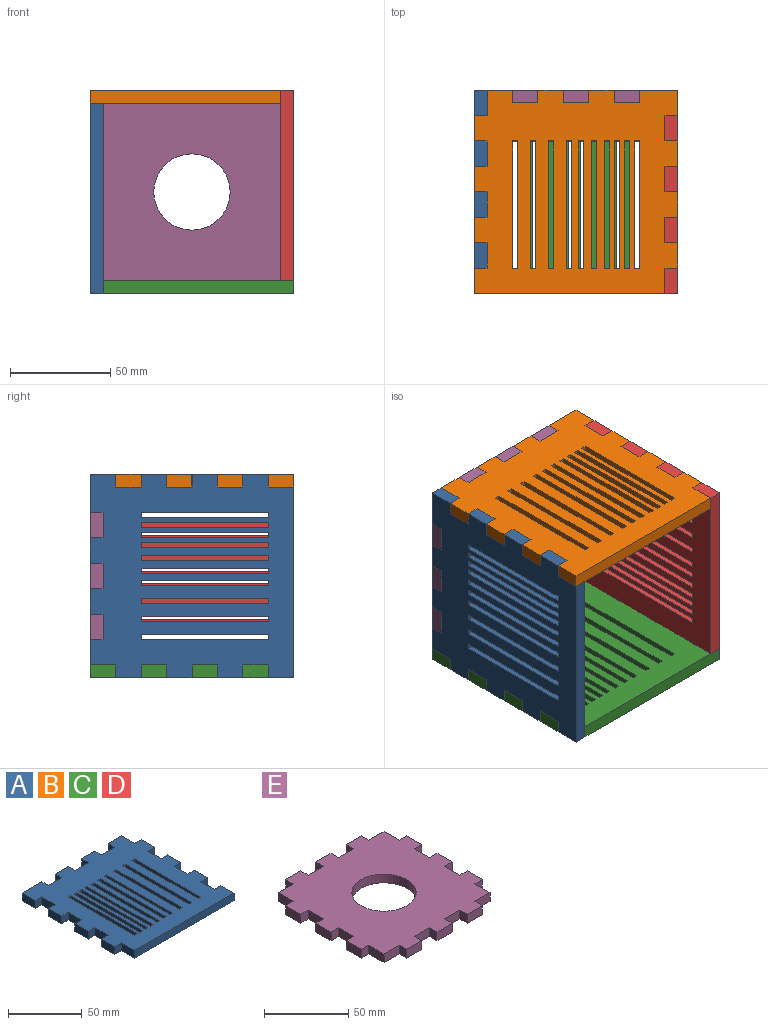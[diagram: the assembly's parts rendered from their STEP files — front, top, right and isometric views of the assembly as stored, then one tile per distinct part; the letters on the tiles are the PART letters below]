
ASSEMBLY  parts=5 mates=4
PART A: 86 faces, bbox 101.6x101.6x6.4 mm
  f0: plane 101.6x101.6mm, normal (0,0,1), area 7822.6mm2, adj f2,f3,f4,f5,f6,f7,f8,f9
  f1: plane 101.6x101.6mm, normal (0,0,-1), area 7822.6mm2, adj f2,f3,f4,f5,f6,f7,f8,f9
  f2: plane 6.35x6.35mm, normal (0,1,0), area 40.3mm2, adj f0,f1,f3,f45
  f3: plane 12.7x6.35mm, normal (1,0,0), area 80.6mm2, adj f0,f1,f2,f4
  f4: plane 6.35x6.35mm, normal (0,-1,0), area 40.3mm2, adj f0,f1,f3,f5
  f5: plane 12.7x6.35mm, normal (1,0,0), area 80.6mm2, adj f0,f1,f4,f6
  f6: plane 6.35x6.35mm, normal (0,1,0), area 40.3mm2, adj f0,f1,f5,f7
  f7: plane 12.7x6.35mm, normal (1,0,0), area 80.6mm2, adj f0,f1,f6,f8
  f8: plane 6.35x6.35mm, normal (0,-1,0), area 40.3mm2, adj f0,f1,f7,f9
  f9: plane 12.7x6.35mm, normal (1,0,0), area 80.6mm2, adj f0,f1,f8,f10
  f10: plane 6.35x6.35mm, normal (0,1,0), area 40.3mm2, adj f0,f1,f9,f11
  f11: plane 12.7x6.35mm, normal (1,0,0), area 80.6mm2, adj f0,f1,f10,f12
  f12: plane 6.35x6.35mm, normal (0,-1,0), area 40.3mm2, adj f0,f1,f11,f13
  f13: plane 12.7x6.35mm, normal (1,0,0), area 80.6mm2, adj f0,f1,f12,f14
  f14: plane 6.35x6.35mm, normal (0,1,0), area 40.3mm2, adj f0,f1,f13,f15
  f15: plane 12.7x6.35mm, normal (1,0,0), area 80.6mm2, adj f0,f1,f14,f16
  f16: plane 12.7x6.35mm, normal (0,1,0), area 80.6mm2, adj f0,f1,f15,f17
  f17: plane 6.35x6.35mm, normal (-1,0,0), area 40.3mm2, adj f0,f1,f16,f18
  f18: plane 12.7x6.35mm, normal (0,1,0), area 80.6mm2, adj f0,f1,f17,f19
  f19: plane 6.35x6.35mm, normal (1,0,0), area 40.3mm2, adj f0,f1,f18,f20
  f20: plane 12.7x6.35mm, normal (0,1,0), area 80.6mm2, adj f0,f1,f19,f21
  f21: plane 6.35x6.35mm, normal (-1,0,0), area 40.3mm2, adj f0,f1,f20,f22
  f22: plane 12.7x6.35mm, normal (0,1,0), area 80.6mm2, adj f0,f1,f21,f23
  f23: plane 6.35x6.35mm, normal (1,0,0), area 40.3mm2, adj f0,f1,f22,f24
  f24: plane 12.7x6.35mm, normal (0,1,0), area 80.6mm2, adj f0,f1,f23,f25
  f25: plane 6.35x6.35mm, normal (-1,0,0), area 40.3mm2, adj f0,f1,f24,f26
  f26: plane 12.7x6.35mm, normal (0,1,0), area 80.6mm2, adj f0,f1,f25,f27
  f27: plane 6.35x6.35mm, normal (1,0,0), area 40.3mm2, adj f0,f1,f26,f28
  f28: plane 19.05x6.35mm, normal (0,1,0), area 121mm2, adj f0,f1,f27,f29
  f29: plane 12.7x6.35mm, normal (-1,0,0), area 80.6mm2, adj f0,f1,f28,f30
  f30: plane 6.35x6.35mm, normal (0,-1,0), area 40.3mm2, adj f0,f1,f29,f31
  f31: plane 12.7x6.35mm, normal (-1,0,0), area 80.6mm2, adj f0,f1,f30,f32
  f32: plane 6.35x6.35mm, normal (0,1,0), area 40.3mm2, adj f0,f1,f31,f33
  f33: plane 12.7x6.35mm, normal (-1,0,0), area 80.6mm2, adj f0,f1,f32,f34
  f34: plane 6.35x6.35mm, normal (0,-1,0), area 40.3mm2, adj f0,f1,f33,f35
  f35: plane 12.7x6.35mm, normal (-1,0,0), area 80.6mm2, adj f0,f1,f34,f36
  f36: plane 6.35x6.35mm, normal (0,1,0), area 40.3mm2, adj f0,f1,f35,f37
  f37: plane 12.7x6.35mm, normal (-1,0,0), area 80.6mm2, adj f0,f1,f36,f38
  f38: plane 6.35x6.35mm, normal (0,-1,0), area 40.3mm2, adj f0,f1,f37,f39
  f39: plane 12.7x6.35mm, normal (-1,0,0), area 80.6mm2, adj f0,f1,f38,f40
  f40: plane 6.35x6.35mm, normal (0,1,0), area 40.3mm2, adj f0,f1,f39,f41
  f41: plane 12.7x6.35mm, normal (-1,0,0), area 80.6mm2, adj f0,f1,f40,f42
  f42: plane 6.35x6.35mm, normal (0,-1,0), area 40.3mm2, adj f0,f1,f41,f43
  f43: plane 12.7x6.35mm, normal (-1,0,0), area 80.6mm2, adj f0,f1,f42,f44
  f44: plane 95.25x6.35mm, normal (0,-1,0), area 604.8mm2, adj f0,f1,f43,f45
  f45: plane 12.7x6.35mm, normal (1,0,0), area 80.6mm2, adj f0,f1,f2,f44
  f46: plane 6.35x2.54mm, normal (0,-1,0), area 16.1mm2, adj f0,f1,f47,f49
  f47: plane 63.5x6.35mm, normal (1,0,0), area 403.2mm2, adj f0,f1,f46,f48
  f48: plane 6.35x2.54mm, normal (0,1,0), area 16.1mm2, adj f0,f1,f47,f49
  f49: plane 63.5x6.35mm, normal (-1,0,0), area 403.2mm2, adj f0,f1,f46,f48
  f50: plane 6.35x2.54mm, normal (0,-1,0), area 16.1mm2, adj f0,f1,f51,f53
  f51: plane 63.5x6.35mm, normal (1,0,0), area 403.2mm2, adj f0,f1,f50,f52
  f52: plane 6.35x2.54mm, normal (0,1,0), area 16.1mm2, adj f0,f1,f51,f53
  f53: plane 63.5x6.35mm, normal (-1,0,0), area 403.2mm2, adj f0,f1,f50,f52
  f54: plane 6.35x2.54mm, normal (0,-1,0), area 16.1mm2, adj f0,f1,f55,f57
  f55: plane 63.5x6.35mm, normal (1,0,0), area 403.2mm2, adj f0,f1,f54,f56
  f56: plane 6.35x2.54mm, normal (0,1,0), area 16.1mm2, adj f0,f1,f55,f57
  f57: plane 63.5x6.35mm, normal (-1,0,0), area 403.2mm2, adj f0,f1,f54,f56
  f58: plane 63.5x6.35mm, normal (1,0,0), area 403.2mm2, adj f0,f1,f59,f61
  f59: plane 6.35x2.54mm, normal (0,1,0), area 16.1mm2, adj f0,f1,f58,f60
  f60: plane 63.5x6.35mm, normal (-1,0,0), area 403.2mm2, adj f0,f1,f59,f61
  f61: plane 6.35x2.54mm, normal (0,-1,0), area 16.1mm2, adj f0,f1,f58,f60
  f62: plane 63.5x6.35mm, normal (1,0,0), area 403.2mm2, adj f0,f1,f63,f65
  f63: plane 6.35x2.54mm, normal (0,1,0), area 16.1mm2, adj f0,f1,f62,f64
  f64: plane 63.5x6.35mm, normal (-1,0,0), area 403.2mm2, adj f0,f1,f63,f65
  f65: plane 6.35x2.54mm, normal (0,-1,0), area 16.1mm2, adj f0,f1,f62,f64
  f66: plane 63.5x6.35mm, normal (1,0,0), area 403.2mm2, adj f0,f1,f67,f69
  f67: plane 6.35x2.54mm, normal (0,1,0), area 16.1mm2, adj f0,f1,f66,f68
  f68: plane 63.5x6.35mm, normal (-1,0,0), area 403.2mm2, adj f0,f1,f67,f69
  f69: plane 6.35x2.54mm, normal (0,-1,0), area 16.1mm2, adj f0,f1,f66,f68
  f70: plane 63.5x6.35mm, normal (1,0,0), area 403.2mm2, adj f0,f1,f71,f73
  f71: plane 6.35x2.54mm, normal (0,1,0), area 16.1mm2, adj f0,f1,f70,f72
  f72: plane 63.5x6.35mm, normal (-1,0,0), area 403.2mm2, adj f0,f1,f71,f73
  f73: plane 6.35x2.54mm, normal (0,-1,0), area 16.1mm2, adj f0,f1,f70,f72
  f74: plane 63.5x6.35mm, normal (1,0,0), area 403.2mm2, adj f0,f1,f75,f77
  f75: plane 6.35x2.54mm, normal (0,1,0), area 16.1mm2, adj f0,f1,f74,f76
  f76: plane 63.5x6.35mm, normal (-1,0,0), area 403.2mm2, adj f0,f1,f75,f77
  f77: plane 6.35x2.54mm, normal (0,-1,0), area 16.1mm2, adj f0,f1,f74,f76
  f78: plane 63.5x6.35mm, normal (1,0,0), area 403.2mm2, adj f0,f1,f79,f81
  f79: plane 6.35x2.54mm, normal (0,1,0), area 16.1mm2, adj f0,f1,f78,f80
  f80: plane 63.5x6.35mm, normal (-1,0,0), area 403.2mm2, adj f0,f1,f79,f81
  f81: plane 6.35x2.54mm, normal (0,-1,0), area 16.1mm2, adj f0,f1,f78,f80
  f82: plane 6.35x2.54mm, normal (0,-1,0), area 16.1mm2, adj f0,f1,f83,f85
  f83: plane 63.5x6.35mm, normal (1,0,0), area 403.2mm2, adj f0,f1,f82,f84
  f84: plane 6.35x2.54mm, normal (0,1,0), area 16.1mm2, adj f0,f1,f83,f85
  f85: plane 63.5x6.35mm, normal (-1,0,0), area 403.2mm2, adj f0,f1,f82,f84
PART B: same geometry as A
PART C: same geometry as A
PART D: same geometry as A
PART E: 55 faces, bbox 101.6x101.6x6.4 mm
  f0: plane 12.7x6.35mm, normal (0,1,0), area 80.6mm2, adj f1,f51,f53,f54
  f1: plane 6.35x6.35mm, normal (-1,0,0), area 40.3mm2, adj f0,f2,f53,f54
  f2: plane 12.7x6.35mm, normal (0,1,0), area 80.6mm2, adj f1,f3,f53,f54
  f3: plane 12.7x6.35mm, normal (-1,0,0), area 80.6mm2, adj f2,f4,f53,f54
  f4: plane 6.35x6.35mm, normal (0,1,0), area 40.3mm2, adj f3,f5,f53,f54
  f5: plane 12.7x6.35mm, normal (-1,0,0), area 80.6mm2, adj f4,f6,f53,f54
  f6: plane 6.35x6.35mm, normal (0,-1,0), area 40.3mm2, adj f5,f7,f53,f54
  f7: plane 12.7x6.35mm, normal (-1,0,0), area 80.6mm2, adj f6,f8,f53,f54
  f8: plane 6.35x6.35mm, normal (0,1,0), area 40.3mm2, adj f7,f9,f53,f54
  f9: plane 12.7x6.35mm, normal (-1,0,0), area 80.6mm2, adj f8,f10,f53,f54
  f10: plane 6.35x6.35mm, normal (0,-1,0), area 40.3mm2, adj f9,f11,f53,f54
  f11: plane 12.7x6.35mm, normal (-1,0,0), area 80.6mm2, adj f10,f12,f53,f54
  f12: plane 6.35x6.35mm, normal (0,1,0), area 40.3mm2, adj f11,f13,f53,f54
  f13: plane 12.7x6.35mm, normal (-1,0,0), area 80.6mm2, adj f12,f14,f53,f54
  f14: plane 6.35x6.35mm, normal (0,-1,0), area 40.3mm2, adj f13,f15,f53,f54
  f15: plane 12.7x6.35mm, normal (-1,0,0), area 80.6mm2, adj f14,f16,f53,f54
  f16: plane 12.7x6.35mm, normal (0,-1,0), area 80.6mm2, adj f15,f17,f53,f54
  f17: plane 6.35x6.35mm, normal (-1,0,0), area 40.3mm2, adj f16,f18,f53,f54
  f18: plane 12.7x6.35mm, normal (0,-1,0), area 80.6mm2, adj f17,f19,f53,f54
  f19: plane 6.35x6.35mm, normal (1,0,0), area 40.3mm2, adj f18,f20,f53,f54
  f20: plane 12.7x6.35mm, normal (0,-1,0), area 80.6mm2, adj f19,f21,f53,f54
  f21: plane 6.35x6.35mm, normal (-1,0,0), area 40.3mm2, adj f20,f22,f53,f54
  f22: plane 12.7x6.35mm, normal (0,-1,0), area 80.6mm2, adj f21,f23,f53,f54
  f23: plane 6.35x6.35mm, normal (1,0,0), area 40.3mm2, adj f22,f24,f53,f54
  f24: plane 12.7x6.35mm, normal (0,-1,0), area 80.6mm2, adj f23,f25,f53,f54
  f25: plane 6.35x6.35mm, normal (-1,0,0), area 40.3mm2, adj f24,f26,f53,f54
  f26: plane 12.7x6.35mm, normal (0,-1,0), area 80.6mm2, adj f25,f27,f53,f54
  f27: plane 6.35x6.35mm, normal (1,0,0), area 40.3mm2, adj f26,f28,f53,f54
  f28: plane 12.7x6.35mm, normal (0,-1,0), area 80.6mm2, adj f27,f29,f53,f54
  f29: plane 12.7x6.35mm, normal (1,0,0), area 80.6mm2, adj f28,f30,f53,f54
  f30: plane 6.35x6.35mm, normal (0,-1,0), area 40.3mm2, adj f29,f31,f53,f54
  f31: plane 12.7x6.35mm, normal (1,0,0), area 80.6mm2, adj f30,f32,f53,f54
  f32: plane 6.35x6.35mm, normal (0,1,0), area 40.3mm2, adj f31,f33,f53,f54
  f33: plane 12.7x6.35mm, normal (1,0,0), area 80.6mm2, adj f32,f34,f53,f54
  f34: plane 6.35x6.35mm, normal (0,-1,0), area 40.3mm2, adj f33,f35,f53,f54
  f35: plane 12.7x6.35mm, normal (1,0,0), area 80.6mm2, adj f34,f36,f53,f54
  f36: plane 6.35x6.35mm, normal (0,1,0), area 40.3mm2, adj f35,f37,f53,f54
  f37: plane 12.7x6.35mm, normal (1,0,0), area 80.6mm2, adj f36,f38,f53,f54
  f38: plane 6.35x6.35mm, normal (0,-1,0), area 40.3mm2, adj f37,f39,f53,f54
  f39: plane 12.7x6.35mm, normal (1,0,0), area 80.6mm2, adj f38,f40,f53,f54
  f40: plane 6.35x6.35mm, normal (0,1,0), area 40.3mm2, adj f39,f41,f53,f54
  f41: plane 12.7x6.35mm, normal (1,0,0), area 80.6mm2, adj f40,f42,f53,f54
  f42: plane 12.7x6.35mm, normal (0,1,0), area 80.6mm2, adj f41,f43,f53,f54
  f43: plane 6.35x6.35mm, normal (1,0,0), area 40.3mm2, adj f42,f44,f53,f54
  f44: plane 12.7x6.35mm, normal (0,1,0), area 80.6mm2, adj f43,f45,f53,f54
  f45: plane 6.35x6.35mm, normal (-1,0,0), area 40.3mm2, adj f44,f46,f53,f54
  f46: plane 12.7x6.35mm, normal (0,1,0), area 80.6mm2, adj f45,f47,f53,f54
  f47: plane 6.35x6.35mm, normal (1,0,0), area 40.3mm2, adj f46,f48,f53,f54
  f48: plane 12.7x6.35mm, normal (0,1,0), area 80.6mm2, adj f47,f49,f53,f54
  f49: plane 6.35x6.35mm, normal (-1,0,0), area 40.3mm2, adj f48,f50,f53,f54
  f50: plane 12.7x6.35mm, normal (0,1,0), area 80.6mm2, adj f49,f51,f53,f54
  f51: plane 6.35x6.35mm, normal (1,0,0), area 40.3mm2, adj f0,f50,f53,f54
  f52: cylinder r=19.05mm len=38.1mm, axis (0,0,-1), area 760.1mm2, adj f53,f54
  f53: plane 101.6x101.6mm, normal (0,0,1), area 7730.9mm2, adj f0,f1,f2,f3,f4,f5,f6,f7
  f54: plane 101.6x101.6mm, normal (0,0,-1), area 7730.9mm2, adj f0,f1,f2,f3,f4,f5,f6,f7
PLACE A rot(axis=(0,1,0),90deg) t=(-59.87,198.83,18.94)mm
PLACE B rot(axis=(0,-1,0),180deg) t=(41.73,198.83,18.94)mm
PLACE C t=(-59.87,198.83,-82.66)mm
PLACE D rot(axis=(0,-1,0),90deg) t=(41.73,198.83,-82.66)mm
PLACE E rot(axis=(-1,0,0),90deg) t=(-59.87,294.08,18.94)mm
MATE fastened E.f39 <-> D.f1  axis (1,0,0) through (41.73,294.08,-63.61)mm
MATE fastened C.f1 <-> E.f44  axis (0,0,-1) through (9.98,294.08,-82.66)mm
MATE fastened B.f1 <-> E.f18  axis (0,0,1) through (-40.82,294.08,18.94)mm
MATE parallel D.f0 <-> A.f0  axis (-1,0,0) through (35.38,249.47,-31.13)mm
